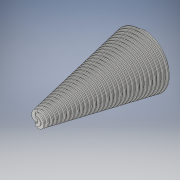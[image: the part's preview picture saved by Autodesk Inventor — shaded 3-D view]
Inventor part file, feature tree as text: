
AUTODESK INVENTOR PART (.ipt)
format: ipt  version: 2018 (Build 220112000, 112)  size: 1,206,784 bytes
history: native  units: in
note: dims shown in document units (in); Inventor stores cm internally (conversion verified against a paired STEP export)
features: sketch x8, extrude x3, helix x2, plane x1, loft x1, hole x1, other x1, projected_geometry x1
ambient origin geometry x8: Origin, YZ Plane, XZ Plane, XY Plane, X Axis, Y Axis, Z Axis, Center Point
bodies: Solid1 (feature_tree)
feature tree (18):
  sketch  "Sketch1"  dims[d0=2.0in d2=3.9in]
  plane  "Work Plane1"
  loft  "Loft1"
  hole  "Hole1"  [1 undecoded]
  other  "Work Axis2"
  sketch  "Sketch6"  dims[d67=1.0in d68=1.0in d11=0.185in d12=0.75in d13=0.375in d14=0.25in d15=0.5635in d16=1.0in d17=0.8108in d41=0.1in]
  helix  "Coil3"  [1 undecoded]
  helix  "Coil4"  [1 undecoded]
  sketch  "Sketch8"  dims[d42=0.1in d43=0.02in]
  sketch  "Sketch9"  dims[d44=0.13in d45=1.0in d46=11.811in d47=-0.0739in d48=90.0deg d49=90.0deg d50=0.0in d51=0.0in]
  extrude  "Extrusion2"  Depth=0.02in
  extrude  "Extrusion3"  Depth=3.775in
  extrude  "Extrusion4"  Depth=0.02in
  sketch  "Sketch2"  dims[d3=0.5in d5=0.0in d6=90.0deg d7=0.0in d8=90.0deg]
  projected_geometry  "Projected Loop1"
  sketch  "Sketch10"  dims[d52=0.13in d53=1.0in d54=11.811in d55=0.0756in d56=90.0deg d57=90.0deg d58=0.0in d59=0.0in d60=3.775in]
  sketch  "Sketch11"  dims[d61=0.02in d62=0.125in]
  sketch  "Sketch12"  dims[d65=0.0in d66=0.5in d69=0.0in d70=0.125in d73=0.02in d74=1.0in d75=0.0in d76=0.02in d77=0.125in d78=1.5in d79=3.0in d80=0.0in d81=0.02in d82=0.0in]
note: 3 required parameter values undecoded (feature->parameter linkage not recoverable at this tier; creation-order binding heuristic only, values carry confidence <= 0.55)
